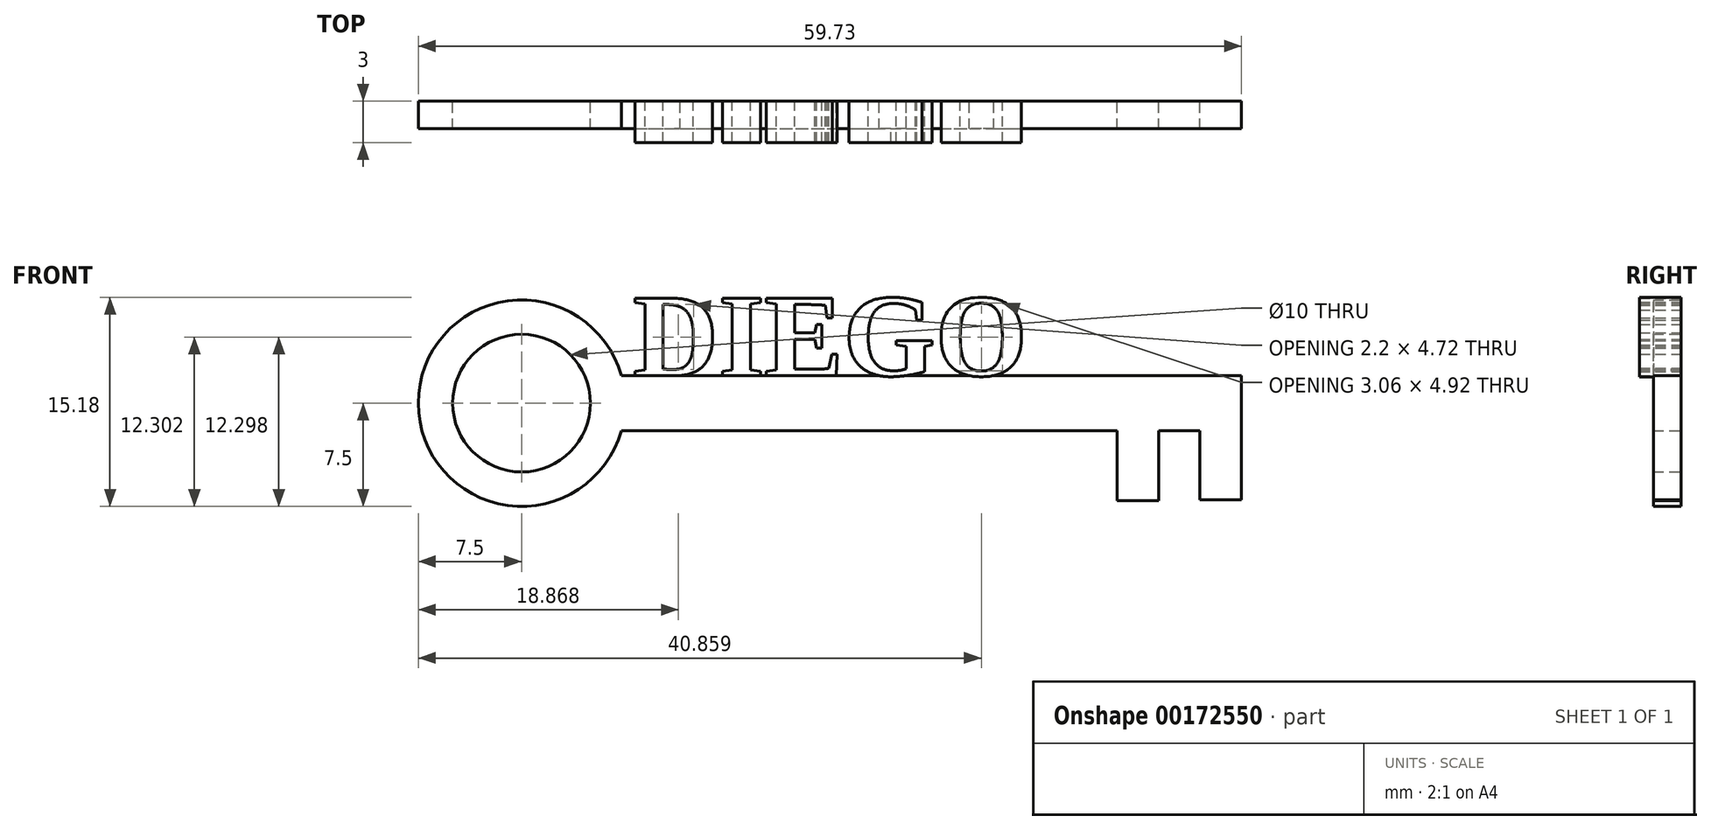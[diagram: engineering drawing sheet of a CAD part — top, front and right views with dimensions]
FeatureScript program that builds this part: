
annotation { "Feature Type Name" : "Feature", "Feature Type Description" : "" }
export const myFeature = defineFeature(function(context is Context, id is Id, definition is map)
    precondition{}
    {
        {
            var Q0;
            Q0=qCreatedBy(makeId("Front.planeOp"),FACE);
            var sketch = newSketch(context, id + "F0", { "sketchPlane" : qUnion([Q0])});
            skArc(sketch, "E0", {"start": v(7.23, 2) * mm, "mid": v(-7.5, 0) * mm, "end": v(7.23, -2) * mm});
            skCircle(sketch, "E1", {"center": v(0, 0) * mm, "radius": 5 * mm});
            skLineSegment(sketch, "E2.bottom", {"start": v(7.23, 2) * mm, "end": v(52.23, 2) * mm});
            skLineSegment(sketch, "E2.top", {"start": v(7.23, -2) * mm, "end": v(43.23, -2) * mm});
            skLineSegment(sketch, "E2.right", {"start": v(52.23, 2) * mm, "end": v(52.23, -2) * mm});
            skLineSegment(sketch, "E3.top", {"start": v(52.23, -7) * mm, "end": v(49.23, -7) * mm});
            skLineSegment(sketch, "E3.left", {"start": v(52.23, -2) * mm, "end": v(52.23, -7) * mm});
            skLineSegment(sketch, "E3.right", {"start": v(49.23, -2) * mm, "end": v(49.23, -7) * mm});
            skLineSegment(sketch, "E4.top", {"start": v(46.23, -7.1) * mm, "end": v(43.23, -7.1) * mm});
            skLineSegment(sketch, "E4.left", {"start": v(46.23, -2) * mm, "end": v(46.23, -7.1) * mm});
            skLineSegment(sketch, "E4.right", {"start": v(43.23, -2) * mm, "end": v(43.23, -7.1) * mm});
            skLineSegment(sketch, "E5.trimOffspring", {"start": v(46.23, -2) * mm, "end": v(49.23, -2) * mm});
            skSolve(sketch);
        }
        {
            var Q0;
            Q0=makeQuery(id+"F0.imprint","IMPRINT",FACE,{"disambiguationData":[TD([[makeQuery(id+"F0.imprint","IMPRINT",EDGE,{"derivedFrom":sQuery(id+"F0.wireOp",EDGE,"E0")}),1.0]])]});
            extrude(context, id + "F1", {"entities" : qUnion([Q0]), "depth" : 2 * mm});
        }
        {
            var Q0;
            Q0=makeQuery(id+"F1.opExtrude","CAP_FACE",FACE,{"disambiguationData":[OSD([sQuery(id+"F0.wireOp",EDGE,"E0"),sQuery(id+"F0.wireOp",EDGE,"E1"),sQuery(id+"F0.wireOp",EDGE,"E2.bottom"),sQuery(id+"F0.wireOp",EDGE,"E2.top"),sQuery(id+"F0.wireOp",EDGE,"E2.right"),sQuery(id+"F0.wireOp",EDGE,"E3.top"),sQuery(id+"F0.wireOp",EDGE,"E3.left"),sQuery(id+"F0.wireOp",EDGE,"E3.right"),sQuery(id+"F0.wireOp",EDGE,"E4.top"),sQuery(id+"F0.wireOp",EDGE,"E4.left"),sQuery(id+"F0.wireOp",EDGE,"E4.right"),sQuery(id+"F0.wireOp",EDGE,"E5.trimOffspring")])],"isStart":false});
            var sketch = newSketch(context, id + "F2", { "sketchPlane" : qUnion([Q0])});
            skText(sketch, "E6", { "text": "DIEGO", "fontName": "Tinos-Bold.ttf"});
            const initialGuessF2  = {"E6": [0.00808, 0.002, 1, 0, 0.00618]};
            skSetInitialGuess(sketch, initialGuessF2);
            skSolve(sketch);
        }
        {
            var Q0;
            Q0 = qSketchRegion(id + "F2", true);
            extrude(context, id + "F3", {"entities" : qUnion([Q0]), "operationType" : NewBodyOperationType.ADD, "depth" : 1 * mm, "hasSecondDirection" : true, "secondDirectionOppositeDirection" : true, "secondDirectionDepth" : 2 * mm});
        }
    });
